# Revit family: FallProtection_DavitBase_Kattsafe_FloorMount_AdhesiveFixed
name_source: partatom
category: Specialty Equipment
units: mm (PartAtom-declared; Revit-internal decimal feet)

## family parameters
Always vertical = Yes
Cut with Voids When Loaded = No
Enable Cutting in Views = No
Maintain Annotation Orientation = No
OmniClass Number = 23.27.71.21
Part Type = Normal
Room Calculation Point = No
Round Connector Dimension = Use Diameter
Shared = No
Work Plane-Based = No

## types (5) — shared parameters
ArmBracketMaterial = Steel_PowderCoat_Kattsafe_Blue
ArmMaterial = Aluminum_Kattsafe_Satin
Assembly Code = E1090100
BaseMaterial = Steel_Stainless_Kattsafe_Satin
Description = Kattsafe davits are designed as a cantilevered anchorage device over balustrades, parapets and curtain walls for rope access work.
ElementType = Fall Protection
Export Type to IFC As = IfcElementComponentType
IfcExportAs = IfcElementComponentType
IfcExportType = USERDEFINED
Manufacturer = Kattsafe®
ManufacturerOverallDepth = 400 mm  [stored 1.31234 ft]
ManufacturerURLProductSpecific = https://kattsafe.com.au
ModifiedIssue = 20240430 $
Type IFC Predefined Type = USERDEFINED
URL = https://kattsafe.com.au
Uniclass2015Code = Pr_40_70_75_21
Uniclass2015Title = Davit arms
Uniclass2015Version = Products v1.23
zero-valued in all types: Default Elevation

## per-type parameters (varying)
| type | ArmHeight | ArmWidth | DavitArmVis | ManufacturerOverallHeight | ManufacturerOverallWidth | ManufacturerSpecCode | Model | OperationalRangeOA | OperationalRangeRadius | RightOffset | Type Comments |
| Base Only (OH520) | 2400 mm | 2506 mm  [stored 8.22178 ft] | No | 266 mm  [stored 0.872703 ft] | 400 mm  [stored 1.31234 ft] | OH520 | OH520 | 1199 mm  [stored 3.93373 ft] | 1070 mm  [stored 3.5105 ft] | 200 mm  [stored 0.656168 ft] | Base Only |
| 1000mm Reach - 1600H (OH510.1600 + OH520) | 1800 mm  [stored 5.90551 ft] | 2106 mm  [stored 6.90945 ft] | Yes | 1850 mm  [stored 6.06955 ft] | 2106 mm  [stored 6.90945 ft] | OH510.1600 + OH520 | OH510.1600 + OH520 | 1199 mm  [stored 3.93373 ft] | 1070 mm  [stored 3.5105 ft] | 907 mm  [stored 2.97572 ft] | 1000mm Reach - 1600mm Height Clearance - Min. 200mm Slab Req. |
| 1000mm Reach - 2200H (OH510.2200 + OH520) | 2400 mm | 2106 mm  [stored 6.90945 ft] | Yes | 2450 mm  [stored 8.03806 ft] | 2106 mm  [stored 6.90945 ft] | OH510.2200 + OH520 | OH510.2200 + OH520 | 1199 mm  [stored 3.93373 ft] | 1070 mm  [stored 3.5105 ft] | 907 mm  [stored 2.97572 ft] | 1000mm Reach - 2200mm Height Clearance - Min. 200mm Slab Req. |
| 1400mm Reach - 1600H (OH514.1600 + OH520) | 1800 mm  [stored 5.90551 ft] | 2506 mm  [stored 8.22178 ft] | Yes | 1850 mm  [stored 6.06955 ft] | 2506 mm  [stored 8.22178 ft] | OH514.1600 + OH520 | OH514.1600 + OH520 | 1599 mm  [stored 5.24606 ft] | 1470 mm | 907 mm  [stored 2.97572 ft] | 1400mm Reach - 1600mm Height Clearance - Min. 220mm Slab Req. |
| 1400mm Reach - 2200H (OH514.2200 + OH520) | 2400 mm | 2506 mm  [stored 8.22178 ft] | Yes | 2450 mm  [stored 8.03806 ft] | 2506 mm  [stored 8.22178 ft] | OH514.2200 + OH520 | OH514.2200 + OH520 | 1599 mm  [stored 5.24606 ft] | 1470 mm | 907 mm  [stored 2.97572 ft] | 1400mm Reach - 2200mm Height Clearance - Min. 220mm Slab Req. |

note: [stored X ft] marks values corroborated as IEEE doubles in the binary element streams (Revit-internal decimal feet)

## geometry (parser evidence)
native form markers: Sweep x7
no freeform markers — native parametric forms only
